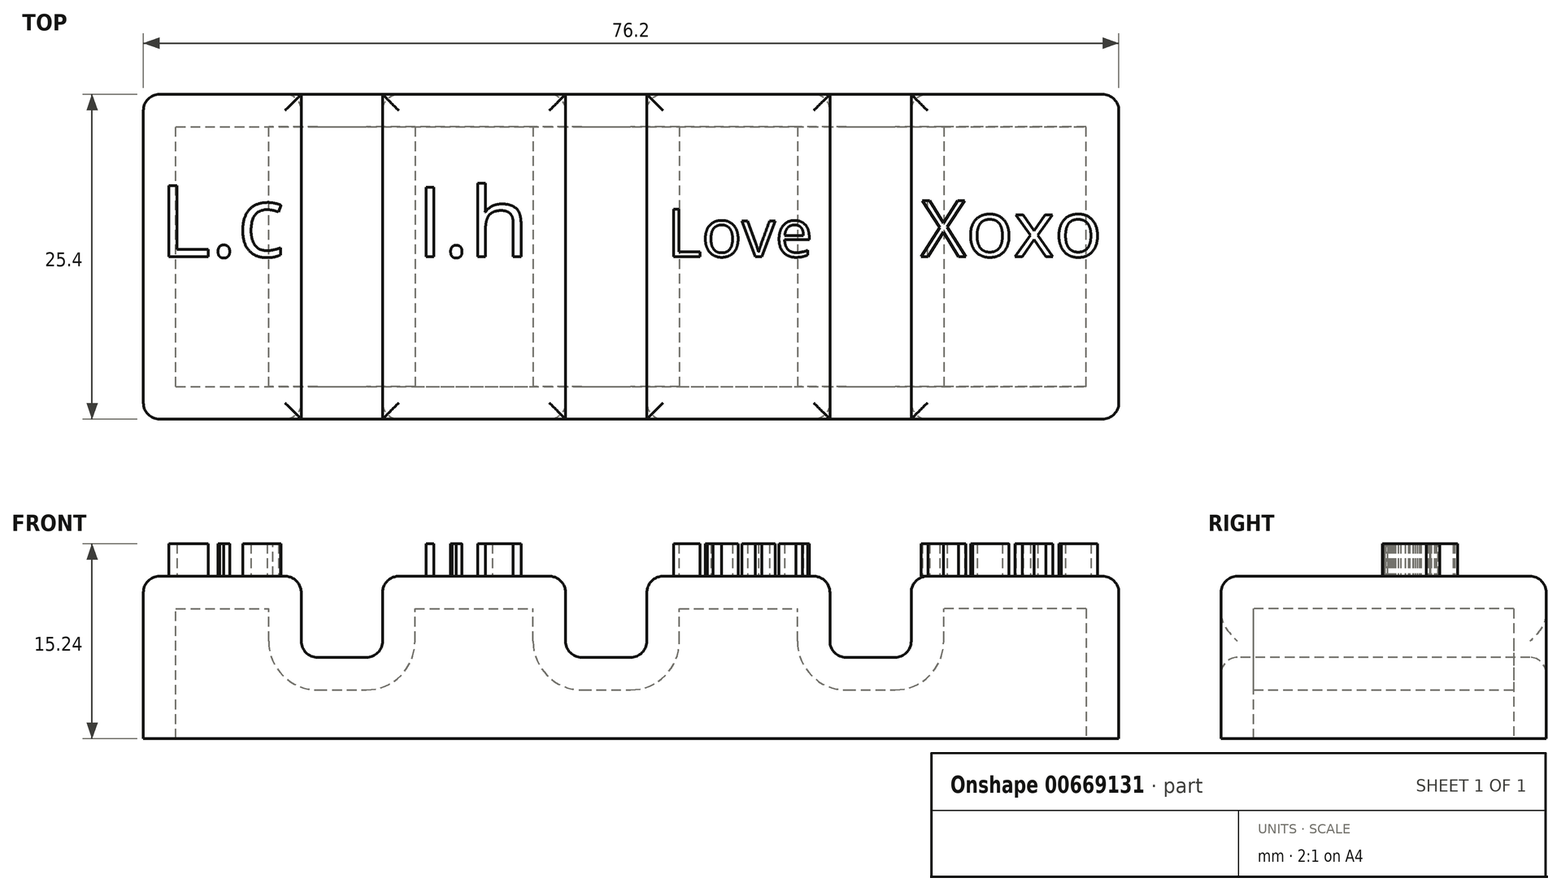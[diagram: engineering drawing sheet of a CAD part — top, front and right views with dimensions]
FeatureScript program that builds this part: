
annotation { "Feature Type Name" : "Feature", "Feature Type Description" : "" }
export const myFeature = defineFeature(function(context is Context, id is Id, definition is map)
    precondition{}
    {
        {
            var Q0;
            Q0=qCreatedBy(makeId("Top.planeOp"),FACE);
            var sketch = newSketch(context, id + "F0", { "sketchPlane" : qUnion([Q0])});
            skLineSegment(sketch, "E0.bottom", {"start": v(-36.16, -12.7) * mm, "end": v(40.04, -12.7) * mm});
            skLineSegment(sketch, "E0.top", {"start": v(-36.16, 12.7) * mm, "end": v(40.04, 12.7) * mm});
            skLineSegment(sketch, "E0.left", {"start": v(-36.16, -12.7) * mm, "end": v(-36.16, 12.7) * mm});
            skLineSegment(sketch, "E0.right", {"start": v(40.04, -12.7) * mm, "end": v(40.04, 12.7) * mm});
            skPoint(sketch, "E0.middle", {"position": v(1.94, 0) * mm});
            skSolve(sketch);
        }
        {
            var Q0;
            Q0=makeQuery(id+"F0.imprint","IMPRINT",FACE,{"disambiguationData":[TD([[makeQuery(id+"F0.imprint","IMPRINT",EDGE,{"derivedFrom":sQuery(id+"F0.wireOp",EDGE,"E0.bottom")}),1.0]])]});
            extrude(context, id + "F1", {"entities" : qUnion([Q0]), "depth" : 12.7 * mm, "offsetDistance" : 25.4 * mm});
        }
        {
            var Q0;
            Q0=makeQuery(id+"F1.opExtrude","SWEPT_FACE",FACE,{"disambiguationData":[OSD([sQuery(id+"F0.wireOp",EDGE,"E0.bottom")])]});
            var sketch = newSketch(context, id + "F2", { "sketchPlane" : qUnion([Q0])});
            skLineSegment(sketch, "E1", {"start": v(-36.16, 6.35) * mm, "end": v(40.04, 6.35) * mm, "construction": true});
            skPoint(sketch, "E2.middle", {"position": v(0, 12.7) * mm});
            skPoint(sketch, "E2.middle.positionSnap0", {"position": v(1.94, 12.7) * mm});
            skPoint(sketch, "E2.centerSnap0", {"position": v(1.94, 12.7) * mm});
            skLineSegment(sketch, "E3.bottom", {"start": v(23.83, 6.35) * mm, "end": v(17.48, 6.35) * mm});
            skLineSegment(sketch, "E3.top", {"start": v(23.83, 19.05) * mm, "end": v(17.48, 19.05) * mm});
            skLineSegment(sketch, "E3.left", {"start": v(23.83, 6.35) * mm, "end": v(23.83, 19.05) * mm});
            skLineSegment(sketch, "E3.right", {"start": v(17.48, 6.35) * mm, "end": v(17.48, 19.05) * mm});
            skPoint(sketch, "E3.middle", {"position": v(20.65, 12.7) * mm});
            skLineSegment(sketch, "E4.bottom", {"start": v(-17.48, 6.35) * mm, "end": v(-23.83, 6.35) * mm});
            skLineSegment(sketch, "E4.top", {"start": v(-17.48, 19.05) * mm, "end": v(-23.83, 19.05) * mm});
            skLineSegment(sketch, "E4.left", {"start": v(-17.48, 6.35) * mm, "end": v(-17.48, 19.05) * mm});
            skLineSegment(sketch, "E4.right", {"start": v(-23.83, 6.35) * mm, "end": v(-23.83, 19.05) * mm});
            skPoint(sketch, "E4.middle", {"position": v(-20.65, 12.7) * mm});
            skLineSegment(sketch, "E5.bottom", {"start": v(3.17, 6.35) * mm, "end": v(-3.18, 6.35) * mm});
            skLineSegment(sketch, "E5.top", {"start": v(3.17, 19.05) * mm, "end": v(-3.18, 19.05) * mm});
            skLineSegment(sketch, "E5.left", {"start": v(3.17, 6.35) * mm, "end": v(3.17, 19.05) * mm});
            skLineSegment(sketch, "E5.right", {"start": v(-3.18, 6.35) * mm, "end": v(-3.18, 19.05) * mm});
            skSolve(sketch);
        }
        {
            var Q0;
            Q0 = qSketchRegion(id + "F2", true);
            extrude(context, id + "F3", {"entities" : qUnion([Q0]), "operationType" : NewBodyOperationType.REMOVE, "endBound" : BoundingType.THROUGH_ALL, "oppositeDirection" : true, "depth" : 25.4 * mm, "offsetDistance" : 25.4 * mm});
        }
        {
            var Q0;
            {var subQ0=sQuery(id+"F0.wireOp",EDGE,"E0.bottom");var subQ1=sQuery(id+"F0.wireOp",EDGE,"E0.top");var subQ2=sQuery(id+"F0.wireOp",EDGE,"E0.left");Q0=makeQuery(id+"F3.boolean.opBoolean","SPLIT",FACE,{"disambiguationData":[TD([makeQuery(id+"F1.opExtrude","SWEPT_FACE",FACE,{"disambiguationData":[OSD([subQ2])]})])],"derivedFrom":makeQuery(id+"F1.opExtrude","CAP_FACE",FACE,{"disambiguationData":[OSD([subQ0,subQ1,subQ2,sQuery(id+"F0.wireOp",EDGE,"E0.right")])],"isStart":false})});}
            var Q1;
            {var subQ0=sQuery(id+"F0.wireOp",EDGE,"E0.bottom");var subQ1=sQuery(id+"F0.wireOp",EDGE,"E0.top");Q1=makeQuery(id+"F3.boolean.opBoolean","SPLIT",FACE,{"disambiguationData":[TD([makeQuery(id+"F3.opExtrude","SWEPT_FACE",FACE,{"disambiguationData":[OSD([sQuery(id+"F2.wireOp",EDGE,"E4.left")])]})])],"derivedFrom":makeQuery(id+"F1.opExtrude","CAP_FACE",FACE,{"disambiguationData":[OSD([subQ0,subQ1,sQuery(id+"F0.wireOp",EDGE,"E0.left"),sQuery(id+"F0.wireOp",EDGE,"E0.right")])],"isStart":false})});}
            var Q2;
            {var subQ0=sQuery(id+"F0.wireOp",EDGE,"E0.bottom");var subQ1=sQuery(id+"F0.wireOp",EDGE,"E0.top");Q2=makeQuery(id+"F3.boolean.opBoolean","SPLIT",FACE,{"disambiguationData":[TD([makeQuery(id+"F3.opExtrude","SWEPT_FACE",FACE,{"disambiguationData":[OSD([sQuery(id+"F2.wireOp",EDGE,"E3.right")])]})])],"derivedFrom":makeQuery(id+"F1.opExtrude","CAP_FACE",FACE,{"disambiguationData":[OSD([subQ0,subQ1,sQuery(id+"F0.wireOp",EDGE,"E0.left"),sQuery(id+"F0.wireOp",EDGE,"E0.right")])],"isStart":false})});}
            var Q3;
            {var subQ0=sQuery(id+"F0.wireOp",EDGE,"E0.bottom");var subQ1=sQuery(id+"F0.wireOp",EDGE,"E0.right");var subQ2=sQuery(id+"F0.wireOp",EDGE,"E0.top");Q3=makeQuery(id+"F3.boolean.opBoolean","SPLIT",FACE,{"disambiguationData":[TD([makeQuery(id+"F1.opExtrude","SWEPT_FACE",FACE,{"disambiguationData":[OSD([subQ1])]})])],"derivedFrom":makeQuery(id+"F1.opExtrude","CAP_FACE",FACE,{"disambiguationData":[OSD([subQ0,subQ2,sQuery(id+"F0.wireOp",EDGE,"E0.left"),subQ1])],"isStart":false})});}
            var Q4;
            Q4=makeQuery(id+"F3.boolean.opBoolean","COPY",FACE,{"derivedFrom":makeQuery(id+"F3.opExtrude","SWEPT_FACE",FACE,{"disambiguationData":[OSD([sQuery(id+"F2.wireOp",EDGE,"E4.bottom")])]})});
            var Q5;
            Q5=makeQuery(id+"F3.boolean.opBoolean","COPY",FACE,{"derivedFrom":makeQuery(id+"F3.opExtrude","SWEPT_FACE",FACE,{"disambiguationData":[OSD([sQuery(id+"F2.wireOp",EDGE,"E5.bottom")])]})});
            var Q6;
            Q6=makeQuery(id+"F3.boolean.opBoolean","COPY",FACE,{"derivedFrom":makeQuery(id+"F3.opExtrude","SWEPT_FACE",FACE,{"disambiguationData":[OSD([sQuery(id+"F2.wireOp",EDGE,"E3.bottom")])]})});
            var Q7;
            Q7=makeQuery(id+"F1.opExtrude","SWEPT_EDGE",EDGE,{"disambiguationData":[OSD([sQuery(id+"F0.wireOp",EDGE,"E0.bottom"),sQuery(id+"F0.wireOp",EDGE,"E0.right")])]});
            var Q8;
            Q8=makeQuery(id+"F1.opExtrude","SWEPT_EDGE",EDGE,{"disambiguationData":[OSD([sQuery(id+"F0.wireOp",EDGE,"E0.top"),sQuery(id+"F0.wireOp",EDGE,"E0.right")])]});
            var Q9;
            Q9=makeQuery(id+"F1.opExtrude","SWEPT_EDGE",EDGE,{"disambiguationData":[OSD([sQuery(id+"F0.wireOp",EDGE,"E0.top"),sQuery(id+"F0.wireOp",EDGE,"E0.left")])]});
            var Q10;
            Q10=makeQuery(id+"F1.opExtrude","SWEPT_EDGE",EDGE,{"disambiguationData":[OSD([sQuery(id+"F0.wireOp",EDGE,"E0.bottom"),sQuery(id+"F0.wireOp",EDGE,"E0.left")])]});
            fillet(context, id + "F4", {"entities" : qUnion([Q0, Q1, Q2, Q3, Q4, Q5, Q6, Q7, Q8, Q9, Q10]), "radius" : 1.27 * mm, "tangentPropagation" : true, "allowEdgeOverflow" : false});
        }
        {
            var Q0;
            Q0=makeQuery(id+"F1.opExtrude","CAP_FACE",FACE,{"disambiguationData":[OSD([sQuery(id+"F0.wireOp",EDGE,"E0.bottom"),sQuery(id+"F0.wireOp",EDGE,"E0.top"),sQuery(id+"F0.wireOp",EDGE,"E0.left"),sQuery(id+"F0.wireOp",EDGE,"E0.right")])],"isStart":true});
            shell(context, id + "F5", {"entities" : qUnion([Q0]), "thickness" : 2.54 * mm});
        }
        {
            var Q0;
            {var subQ0=sQuery(id+"F0.wireOp",EDGE,"E0.bottom");var subQ1=sQuery(id+"F0.wireOp",EDGE,"E0.top");var subQ2=sQuery(id+"F0.wireOp",EDGE,"E0.left");Q0=makeQuery(id+"F3.boolean.opBoolean","SPLIT",FACE,{"disambiguationData":[TD([makeQuery(id+"F1.opExtrude","SWEPT_FACE",FACE,{"disambiguationData":[OSD([subQ2])]})])],"derivedFrom":makeQuery(id+"F1.opExtrude","CAP_FACE",FACE,{"disambiguationData":[OSD([subQ0,subQ1,subQ2,sQuery(id+"F0.wireOp",EDGE,"E0.right")])],"isStart":false})});}
            var sketch = newSketch(context, id + "F6", { "sketchPlane" : qUnion([Q0])});
            skText(sketch, "E6", { "text": "L.c", "fontName": "OpenSans-Regular.ttf"});
            const initialGuessF6  = {"E6": [-0.03494, 0, 1, 0, 0.0056]};
            skSetInitialGuess(sketch, initialGuessF6);
            skSolve(sketch);
        }
        {
            var Q0;
            {var subQ0=sQuery(id+"F0.wireOp",EDGE,"E0.bottom");var subQ1=sQuery(id+"F0.wireOp",EDGE,"E0.top");Q0=makeQuery(id+"F3.boolean.opBoolean","SPLIT",FACE,{"disambiguationData":[TD([makeQuery(id+"F3.opExtrude","SWEPT_FACE",FACE,{"disambiguationData":[OSD([sQuery(id+"F2.wireOp",EDGE,"E4.left")])]})])],"derivedFrom":makeQuery(id+"F1.opExtrude","CAP_FACE",FACE,{"disambiguationData":[OSD([subQ0,subQ1,sQuery(id+"F0.wireOp",EDGE,"E0.left"),sQuery(id+"F0.wireOp",EDGE,"E0.right")])],"isStart":false})});}
            var sketch = newSketch(context, id + "F7", { "sketchPlane" : qUnion([Q0])});
            skText(sketch, "E7", { "text": "I.h", "fontName": "OpenSans-Regular.ttf"});
            const initialGuessF7  = {"E7": [-0.01483, 0, 1, 0, 0.00546]};
            skSetInitialGuess(sketch, initialGuessF7);
            skSolve(sketch);
        }
        {
            var Q0;
            {var subQ0=sQuery(id+"F0.wireOp",EDGE,"E0.bottom");var subQ1=sQuery(id+"F0.wireOp",EDGE,"E0.top");Q0=makeQuery(id+"F3.boolean.opBoolean","SPLIT",FACE,{"disambiguationData":[TD([makeQuery(id+"F3.opExtrude","SWEPT_FACE",FACE,{"disambiguationData":[OSD([sQuery(id+"F2.wireOp",EDGE,"E3.right")])]})])],"derivedFrom":makeQuery(id+"F1.opExtrude","CAP_FACE",FACE,{"disambiguationData":[OSD([subQ0,subQ1,sQuery(id+"F0.wireOp",EDGE,"E0.left"),sQuery(id+"F0.wireOp",EDGE,"E0.right")])],"isStart":false})});}
            var sketch = newSketch(context, id + "F8", { "sketchPlane" : qUnion([Q0])});
            skText(sketch, "E8", { "text": "Love", "fontName": "OpenSans-Regular.ttf"});
            const initialGuessF8  = {"E8": [0.00475, 0, 1, 0, 0.00375]};
            skSetInitialGuess(sketch, initialGuessF8);
            skSolve(sketch);
        }
        {
            var Q0;
            {var subQ0=sQuery(id+"F0.wireOp",EDGE,"E0.bottom");var subQ1=sQuery(id+"F0.wireOp",EDGE,"E0.right");var subQ2=sQuery(id+"F0.wireOp",EDGE,"E0.top");Q0=makeQuery(id+"F3.boolean.opBoolean","SPLIT",FACE,{"disambiguationData":[TD([makeQuery(id+"F1.opExtrude","SWEPT_FACE",FACE,{"disambiguationData":[OSD([subQ1])]})])],"derivedFrom":makeQuery(id+"F1.opExtrude","CAP_FACE",FACE,{"disambiguationData":[OSD([subQ0,subQ2,sQuery(id+"F0.wireOp",EDGE,"E0.left"),subQ1])],"isStart":false})});}
            var sketch = newSketch(context, id + "F9", { "sketchPlane" : qUnion([Q0])});
            skText(sketch, "E9", { "text": "Xoxo", "fontName": "OpenSans-Regular.ttf"});
            const initialGuessF9  = {"E9": [0.02458, 0, 1, 0, 0.00441]};
            skSetInitialGuess(sketch, initialGuessF9);
            skSolve(sketch);
        }
        {
            var Q0;
            Q0 = qSketchRegion(id + "F6", true);
            extrude(context, id + "F10", {"entities" : qUnion([Q0]), "operationType" : NewBodyOperationType.ADD, "depth" : 2.54 * mm, "offsetDistance" : 25.4 * mm});
        }
        {
            var Q0;
            Q0 = qSketchRegion(id + "F7", true);
            extrude(context, id + "F11", {"entities" : qUnion([Q0]), "operationType" : NewBodyOperationType.ADD, "depth" : 2.54 * mm, "offsetDistance" : 25.4 * mm});
        }
        {
            var Q0;
            Q0 = qSketchRegion(id + "F8", true);
            extrude(context, id + "F12", {"entities" : qUnion([Q0]), "operationType" : NewBodyOperationType.ADD, "depth" : 2.54 * mm, "offsetDistance" : 25.4 * mm});
        }
        {
            var Q0;
            Q0 = qSketchRegion(id + "F9", true);
            extrude(context, id + "F13", {"entities" : qUnion([Q0]), "operationType" : NewBodyOperationType.ADD, "depth" : 2.54 * mm, "offsetDistance" : 25.4 * mm});
        }
    });
